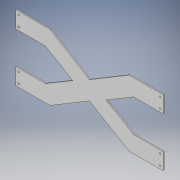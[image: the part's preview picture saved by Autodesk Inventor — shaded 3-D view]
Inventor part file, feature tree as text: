
AUTODESK INVENTOR PART (.ipt)
format: ipt  version: 2017 SP1 (Build 210196100, 196)  size: 135,680 bytes
history: native  units: in
note: dims shown in document units (in); Inventor stores cm internally (conversion verified against a paired STEP export)
features: extrude x1, sketch x1, projected_geometry x1, other x1
ambient origin geometry x8: Origin, YZ Plane, XZ Plane, XY Plane, X Axis, Y Axis, Z Axis, Center Point
bodies: Solid1 (feature_tree)
feature tree (4):
  extrude  "Extrusion1"  Depth=0.375in
  sketch  "Sketch1"  dims[d0=0.2in d1=0.375in d3=17.25in d4=1.0in d5=0.0in]
  projected_geometry  "Projected Loop1"
  other  "tube frame"
